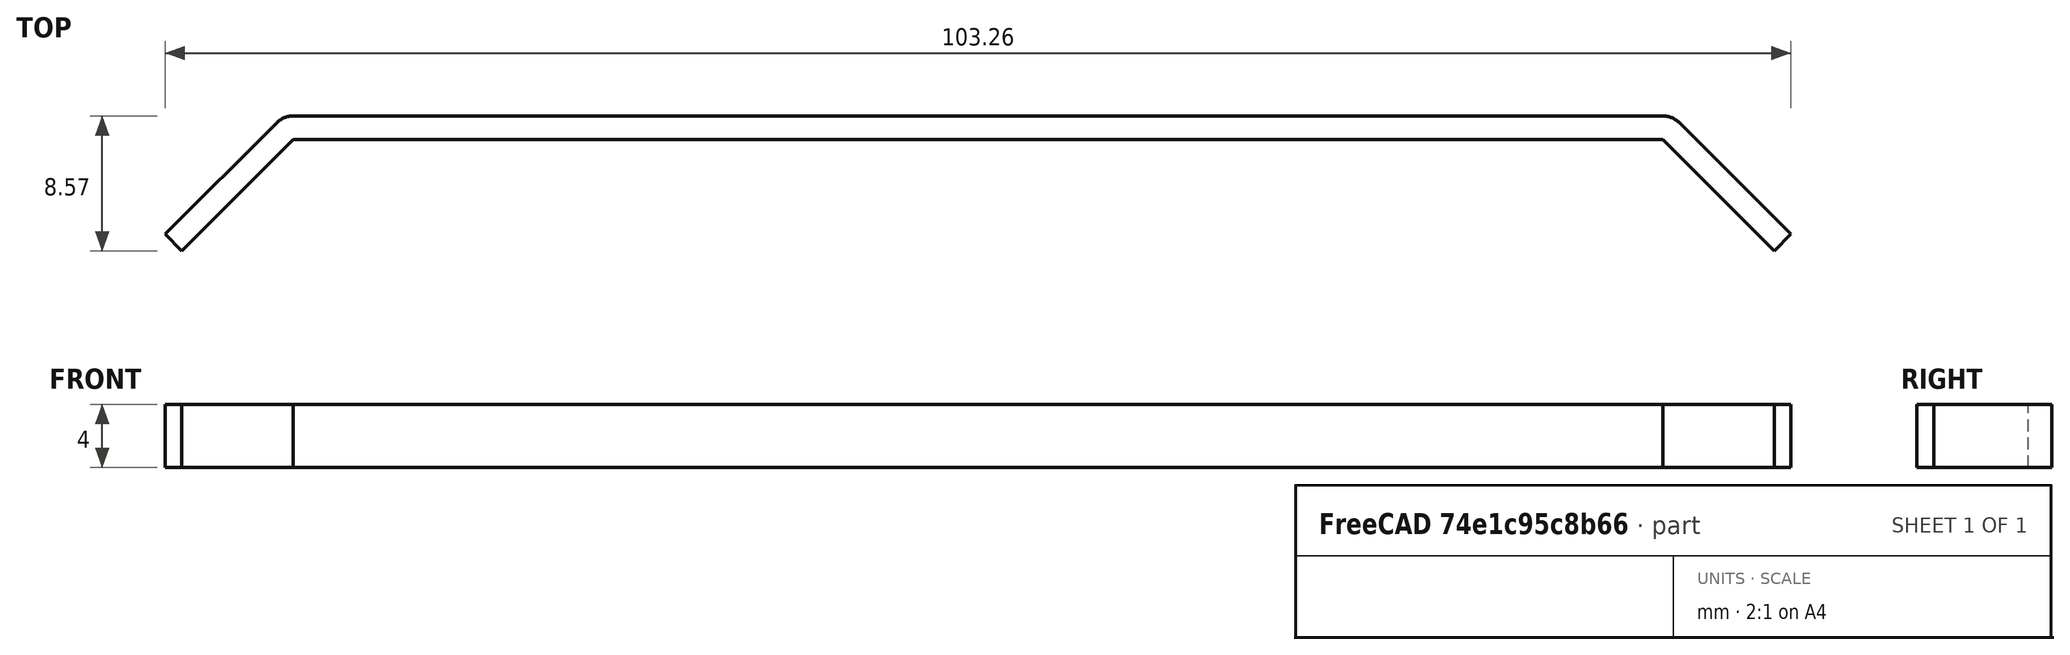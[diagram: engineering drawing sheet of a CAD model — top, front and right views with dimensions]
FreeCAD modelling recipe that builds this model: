
FCSTD DOCUMENT  (FreeCAD 0.16R6348 (Git))
Label: Bumper
License: All rights reserved
LicenseURL: http://en.wikipedia.org/wiki/All_rights_reserved
objects: Sketcher::SketchObject×1, PartDesign::Pad×1
note: 3 computed .brp shape members not serialized (recipe doc carries the construction recipe); baked Part::Feature solids carry a one-line shape summary decoded from their .brp

FEATURE [Sketcher::SketchObject] Sketch
  sketch-geometry (10):
    g0: LineSegment StartX=-43.5 StartY=5.33374 StartZ=0 EndX=43.5 EndY=5.33374 EndZ=0
    g1: LineSegment StartX=-43.5 StartY=6.83374 StartZ=0 EndX=43.5 EndY=6.83374 EndZ=0
    g2: LineSegment StartX=-44.5607 StartY=6.3944 StartZ=0 EndX=-51.6317 EndY=-0.676671 EndZ=0
    g3: LineSegment StartX=-51.6317 StartY=-0.676671 StartZ=0 EndX=-50.5711 EndY=-1.73733 EndZ=0
    g4: LineSegment StartX=-50.5711 StartY=-1.73733 StartZ=0 EndX=-43.5 EndY=5.33374 EndZ=0
    g5: ArcOfCircle CenterX=-43.5 CenterY=5.33374 CenterZ=0 NormalX=0 NormalY=0 NormalZ=1 Radius=1.5 StartAngle=1.5708 EndAngle=2.35619
    g6: LineSegment StartX=43.5 StartY=5.33374 StartZ=0 EndX=50.5711 EndY=-1.73733 EndZ=0
    g7: LineSegment StartX=50.5711 StartY=-1.73733 StartZ=0 EndX=51.6317 EndY=-0.676671 EndZ=0
    g8: LineSegment StartX=51.6317 StartY=-0.676671 StartZ=0 EndX=44.5607 EndY=6.3944 EndZ=0
    g9: ArcOfCircle CenterX=43.5 CenterY=5.33374 CenterZ=0 NormalX=0 NormalY=0 NormalZ=1 Radius=1.5 StartAngle=0.785398 EndAngle=1.5708
  constraints (27):
    c: DistanceY(g0,g1) = 1.5
    c: Symmetric(g1,g1,g-2)
    c: Symmetric(g0,g0,g-2)
    c: Equal(g1,g0)
    c: Distance(g1) = 87
    c: Coincident(g2,g3)
    c: Coincident(g3,g4)
    c: Perpendicular(g3,g4)
    c: Perpendicular(g3,g2)
    c: Equal(g4,g2)
    c: Coincident(g4,g0)
    c: Angle(g4,g0) = 2.35619
    c: Distance(g3) = 1.5
    c: Distance(g2) = 10
    c: Coincident(g5,g0)
    c: Coincident(g5,g2)
    c: Coincident(g5,g1)
    c: Coincident(g6,g7)
    c: Coincident(g7,g8)
    c: Perpendicular(g7,g6)
    c: Perpendicular(g8,g7)
    c: Equal(g6,g8)
    c: Coincident(g6,g0)
    c: Symmetric(g6,g3,g-2)
    c: Coincident(g9,g0)
    c: Coincident(g9,g1)
    c: Coincident(g9,g8)
FEATURE [PartDesign::Pad] Pad
  Length = 4
  Length2 = 100
  Sketch = -> Sketch
  Type = 0
